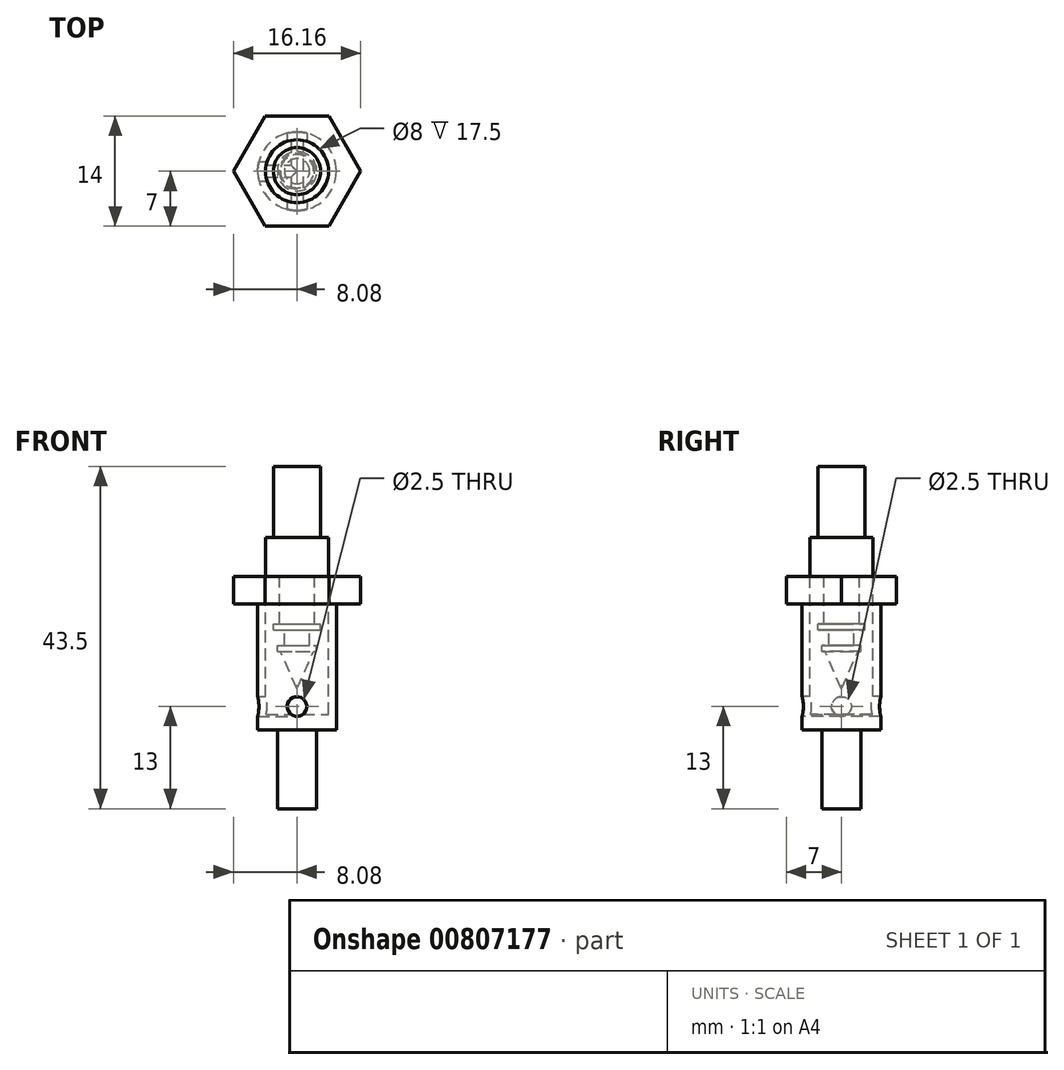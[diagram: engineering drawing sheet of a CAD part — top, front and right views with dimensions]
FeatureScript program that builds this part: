
annotation { "Feature Type Name" : "Feature", "Feature Type Description" : "" }
export const myFeature = defineFeature(function(context is Context, id is Id, definition is map)
    precondition{}
    {
        {
            var Q0;
            Q0=qCreatedBy(makeId("Top.planeOp"),FACE);
            var sketch = newSketch(context, id + "F0", { "sketchPlane" : qUnion([Q0])});
            skCircle(sketch, "E0", {"center": v(0, 0) * mm, "radius": 2.5 * mm});
            skSolve(sketch);
        }
        {
            var Q0;
            Q0 = qSketchRegion(id + "F0", true);
            extrude(context, id + "F1", {"entities" : qUnion([Q0]), "depth" : 10 * mm, "offsetDistance" : 25 * mm});
        }
        {
            var Q0;
            Q0=makeQuery(id+"F1.opExtrude","CAP_FACE",FACE,{"disambiguationData":[OSD([sQuery(id+"F0.wireOp",EDGE,"E0")])],"isStart":false});
            var sketch = newSketch(context, id + "F2", { "sketchPlane" : qUnion([Q0])});
            skCircle(sketch, "E1", {"center": v(0, 0) * mm, "radius": 5 * mm});
            skSolve(sketch);
        }
        {
            var Q0;
            Q0 = qSketchRegion(id + "F2", true);
            extrude(context, id + "F3", {"entities" : qUnion([Q0]), "operationType" : NewBodyOperationType.ADD, "depth" : 16 * mm, "offsetDistance" : 25 * mm});
        }
        {
            var Q0;
            Q0=makeQuery(id+"F3.opExtrude","CAP_FACE",FACE,{"disambiguationData":[OSD([sQuery(id+"F2.wireOp",EDGE,"E1")])],"isStart":false});
            var sketch = newSketch(context, id + "F4", { "sketchPlane" : qUnion([Q0])});
            skCircle(sketch, "E2.cCircle", {"center": v(0, 0) * mm, "radius": 7 * mm, "construction": true});
            skLineSegment(sketch, "E2.0", {"start": v(-4.04, 7) * mm, "end": v(4.04, 7) * mm});
            skLineSegment(sketch, "E2.1", {"start": v(4.04, 7) * mm, "end": v(8.08, 0) * mm});
            skLineSegment(sketch, "E2.2", {"start": v(8.08, 0) * mm, "end": v(4.04, -7) * mm});
            skLineSegment(sketch, "E2.3", {"start": v(4.04, -7) * mm, "end": v(-4.04, -7) * mm});
            skLineSegment(sketch, "E2.4", {"start": v(-4.04, -7) * mm, "end": v(-8.08, 0) * mm});
            skLineSegment(sketch, "E2.5", {"start": v(-8.08, 0) * mm, "end": v(-4.04, 7) * mm});
            skPoint(sketch, "E2.0.midPoint", {"position": v(0, 7) * mm});
            skSolve(sketch);
        }
        {
            var Q0;
            Q0 = qSketchRegion(id + "F4", true);
            extrude(context, id + "F5", {"entities" : qUnion([Q0]), "operationType" : NewBodyOperationType.ADD, "depth" : 3.5 * mm, "offsetDistance" : 25 * mm});
        }
        {
            var Q0;
            Q0=makeQuery(id+"F5.opExtrude","CAP_FACE",FACE,{"disambiguationData":[OSD([sQuery(id+"F4.wireOp",EDGE,"E2.0"),sQuery(id+"F4.wireOp",EDGE,"E2.1"),sQuery(id+"F4.wireOp",EDGE,"E2.2"),sQuery(id+"F4.wireOp",EDGE,"E2.3"),sQuery(id+"F4.wireOp",EDGE,"E2.4"),sQuery(id+"F4.wireOp",EDGE,"E2.5")])],"isStart":false});
            var sketch = newSketch(context, id + "F6", { "sketchPlane" : qUnion([Q0])});
            skCircle(sketch, "E3", {"center": v(0, 0) * mm, "radius": 4 * mm});
            skSolve(sketch);
        }
        {
            var Q0;
            Q0 = qSketchRegion(id + "F6", true);
            extrude(context, id + "F7", {"entities" : qUnion([Q0]), "operationType" : NewBodyOperationType.REMOVE, "oppositeDirection" : true, "depth" : 17.5 * mm, "offsetDistance" : 25 * mm});
        }
        {
            var Q0;
            Q0=qCreatedBy(makeId("Front.planeOp"),FACE);
            var sketch = newSketch(context, id + "F8", { "sketchPlane" : qUnion([Q0])});
            skCircle(sketch, "E4", {"center": v(0, 13) * mm, "radius": 1.25 * mm});
            skSolve(sketch);
        }
        {
            var Q0;
            Q0 = qSketchRegion(id + "F8", true);
            extrude(context, id + "F9", {"entities" : qUnion([Q0]), "operationType" : NewBodyOperationType.REMOVE, "endBound" : BoundingType.SYMMETRIC, "oppositeDirection" : true, "depth" : 25 * mm, "offsetDistance" : 25 * mm});
        }
        {
            var Q0;
            Q0=qCreatedBy(makeId("Right.planeOp"),FACE);
            var sketch = newSketch(context, id + "F10", { "sketchPlane" : qUnion([Q0])});
            skCircle(sketch, "E5", {"center": v(0, 13) * mm, "radius": 1.25 * mm});
            skSolve(sketch);
        }
        {
            var Q0;
            Q0 = qSketchRegion(id + "F10", true);
            extrude(context, id + "F11", {"entities" : qUnion([Q0]), "operationType" : NewBodyOperationType.REMOVE, "endBound" : BoundingType.THROUGH_ALL, "oppositeDirection" : true, "depth" : 25 * mm, "offsetDistance" : 25 * mm});
        }
        {
            var Q0;
            Q0=makeQuery(id+"F5.opExtrude","CAP_FACE",FACE,{"disambiguationData":[OSD([sQuery(id+"F4.wireOp",EDGE,"E2.0"),sQuery(id+"F4.wireOp",EDGE,"E2.1"),sQuery(id+"F4.wireOp",EDGE,"E2.2"),sQuery(id+"F4.wireOp",EDGE,"E2.3"),sQuery(id+"F4.wireOp",EDGE,"E2.4"),sQuery(id+"F4.wireOp",EDGE,"E2.5")])],"isStart":false});
            var sketch = newSketch(context, id + "F12", { "sketchPlane" : qUnion([Q0])});
            skCircle(sketch, "E6", {"center": v(0, 0) * mm, "radius": 4 * mm});
            skSolve(sketch);
        }
        {
            var Q0;
            Q0 = qSketchRegion(id + "F12", true);
            extrude(context, id + "F13", {"entities" : qUnion([Q0]), "depth" : 5 * mm, "offsetDistance" : 25 * mm});
        }
        {
            var Q0;
            Q0=makeQuery(id+"F13.opExtrude","CAP_FACE",FACE,{"disambiguationData":[OSD([sQuery(id+"F12.wireOp",EDGE,"E6")])],"isStart":false});
            var sketch = newSketch(context, id + "F14", { "sketchPlane" : qUnion([Q0])});
            skCircle(sketch, "E7", {"center": v(0, 0) * mm, "radius": 3 * mm});
            skSolve(sketch);
        }
        {
            var Q0;
            Q0 = qSketchRegion(id + "F14", true);
            extrude(context, id + "F15", {"entities" : qUnion([Q0]), "operationType" : NewBodyOperationType.ADD, "depth" : 9 * mm, "offsetDistance" : 25 * mm});
        }
        {
            var Q0;
            Q0=makeQuery(id+"F13.opExtrude","CAP_FACE",FACE,{"disambiguationData":[OSD([sQuery(id+"F12.wireOp",EDGE,"E6")])],"isStart":true});
            var sketch = newSketch(context, id + "F16", { "sketchPlane" : qUnion([Q0])});
            skCircle(sketch, "E8", {"center": v(0, 0) * mm, "radius": 2.25 * mm});
            skSolve(sketch);
        }
        {
            var Q0;
            Q0 = qSketchRegion(id + "F16", true);
            extrude(context, id + "F17", {"entities" : qUnion([Q0]), "operationType" : NewBodyOperationType.ADD, "depth" : 6 * mm, "offsetDistance" : 25 * mm});
        }
        {
            var Q0;
            Q0=makeQuery(id+"F17.opExtrude","CAP_FACE",FACE,{"disambiguationData":[OSD([sQuery(id+"F16.wireOp",EDGE,"E8")])],"isStart":false});
            var sketch = newSketch(context, id + "F18", { "sketchPlane" : qUnion([Q0])});
            skCircle(sketch, "E9", {"center": v(0, 0) * mm, "radius": 3 * mm});
            skSolve(sketch);
        }
        {
            var Q0;
            Q0 = qSketchRegion(id + "F18", true);
            extrude(context, id + "F19", {"entities" : qUnion([Q0]), "operationType" : NewBodyOperationType.ADD, "depth" : 0.75 * mm, "offsetDistance" : 25 * mm});
        }
        {
            var Q0;
            Q0=makeQuery(id+"F19.opExtrude","CAP_FACE",FACE,{"disambiguationData":[OSD([sQuery(id+"F18.wireOp",EDGE,"E9")])],"isStart":false});
            var sketch = newSketch(context, id + "F20", { "sketchPlane" : qUnion([Q0])});
            skCircle(sketch, "E10", {"center": v(0, 0) * mm, "radius": 1.6 * mm});
            skSolve(sketch);
        }
        {
            var Q0;
            Q0 = qSketchRegion(id + "F20", true);
            extrude(context, id + "F21", {"entities" : qUnion([Q0]), "operationType" : NewBodyOperationType.ADD, "depth" : 2 * mm, "offsetDistance" : 25 * mm});
        }
        {
            var Q0;
            Q0=makeQuery(id+"F21.opExtrude","CAP_FACE",FACE,{"disambiguationData":[OSD([sQuery(id+"F20.wireOp",EDGE,"E10")])],"isStart":false});
            var sketch = newSketch(context, id + "F22", { "sketchPlane" : qUnion([Q0])});
            skCircle(sketch, "E11", {"center": v(0, 0) * mm, "radius": 2.5 * mm});
            skSolve(sketch);
        }
        {
            var Q0;
            Q0 = qSketchRegion(id + "F22", true);
            extrude(context, id + "F23", {"entities" : qUnion([Q0]), "operationType" : NewBodyOperationType.ADD, "depth" : 0.75 * mm, "offsetDistance" : 25 * mm});
        }
        {
            var Q0;
            Q0=qCreatedBy(makeId("Front.planeOp"),FACE);
            var sketch = newSketch(context, id + "F24", { "sketchPlane" : qUnion([Q0])});
            skLineSegment(sketch, "E12.0", {"start": v(2.5, 20) * mm, "end": v(-2.5, 20) * mm});
            skLineSegment(sketch, "E13", {"start": v(0, 15.25) * mm, "end": v(-2.11, 20) * mm});
            skLineSegment(sketch, "E14", {"start": v(0, 15.25) * mm, "end": v(0, 20) * mm, "construction": true});
            skLineSegment(sketch, "E15", {"start": v(-2.11, 20) * mm, "end": v(0, 20) * mm});
            skLineSegment(sketch, "E16", {"start": v(0, 15.25) * mm, "end": v(0, 20) * mm});
            skSolve(sketch);
        }
        {
            var Q0;
            Q0=makeQuery(id+"F24.imprint","IMPRINT",FACE,{"disambiguationData":[TD([[makeQuery(id+"F24.imprint","IMPRINT",EDGE,{"derivedFrom":sQuery(id+"F24.wireOp",EDGE,"E13")}),-1.0]])]});
            var Q1;
            Q1=sQuery(id+"F24.wireOp",EDGE,"E16");
            revolve(context, id + "F25", {"operationType" : NewBodyOperationType.ADD, "surfaceOperationType" : NewSurfaceOperationType.NEW, "entities" : qUnion([Q0]), "axis" : qUnion([Q1]), "revolveType" : RevolveType.FULL});
        }
    });
